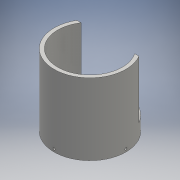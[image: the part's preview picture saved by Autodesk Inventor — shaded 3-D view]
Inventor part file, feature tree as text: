
AUTODESK INVENTOR PART (.ipt)
format: ipt  version: 2016 (Build 200138000, 138)  size: 146,944 bytes
history: native  units: mm
features: extrude x6, sketch x6, other x5
ambient origin geometry x8: Origin, YZ Plane, XZ Plane, XY Plane, X Axis, Y Axis, Z Axis, Center Point
bodies: Body1 (feature_tree)
feature tree (17):
  other  "ソリッド1"
  extrude  "押し出し1"  Depth=90.0mm
  extrude  "押し出し2"  Depth=100.0mm
  other  "作業平面1"
  extrude  "押し出し3"  Depth=20.0mm TaperAngle=0.0deg
  other  "作業平面2"
  other  "作業平面3"
  other  "作業平面4"
  extrude  "押し出し4"  TaperAngle=150.0deg  [1 undecoded]
  extrude  "押し出し5"  TaperAngle=30.0deg  [1 undecoded]
  extrude  "押し出し6"  Depth=80.0mm TaperAngle=0.0deg
  sketch  "スケッチ1"
  sketch  "スケッチ2"
  sketch  "スケッチ3"
  sketch  "スケッチ4"
  sketch  "スケッチ5"
  sketch  "スケッチ6"
note: 2 required parameter values undecoded (feature->parameter linkage not recoverable at this tier; creation-order binding heuristic only, values carry confidence <= 0.55)
